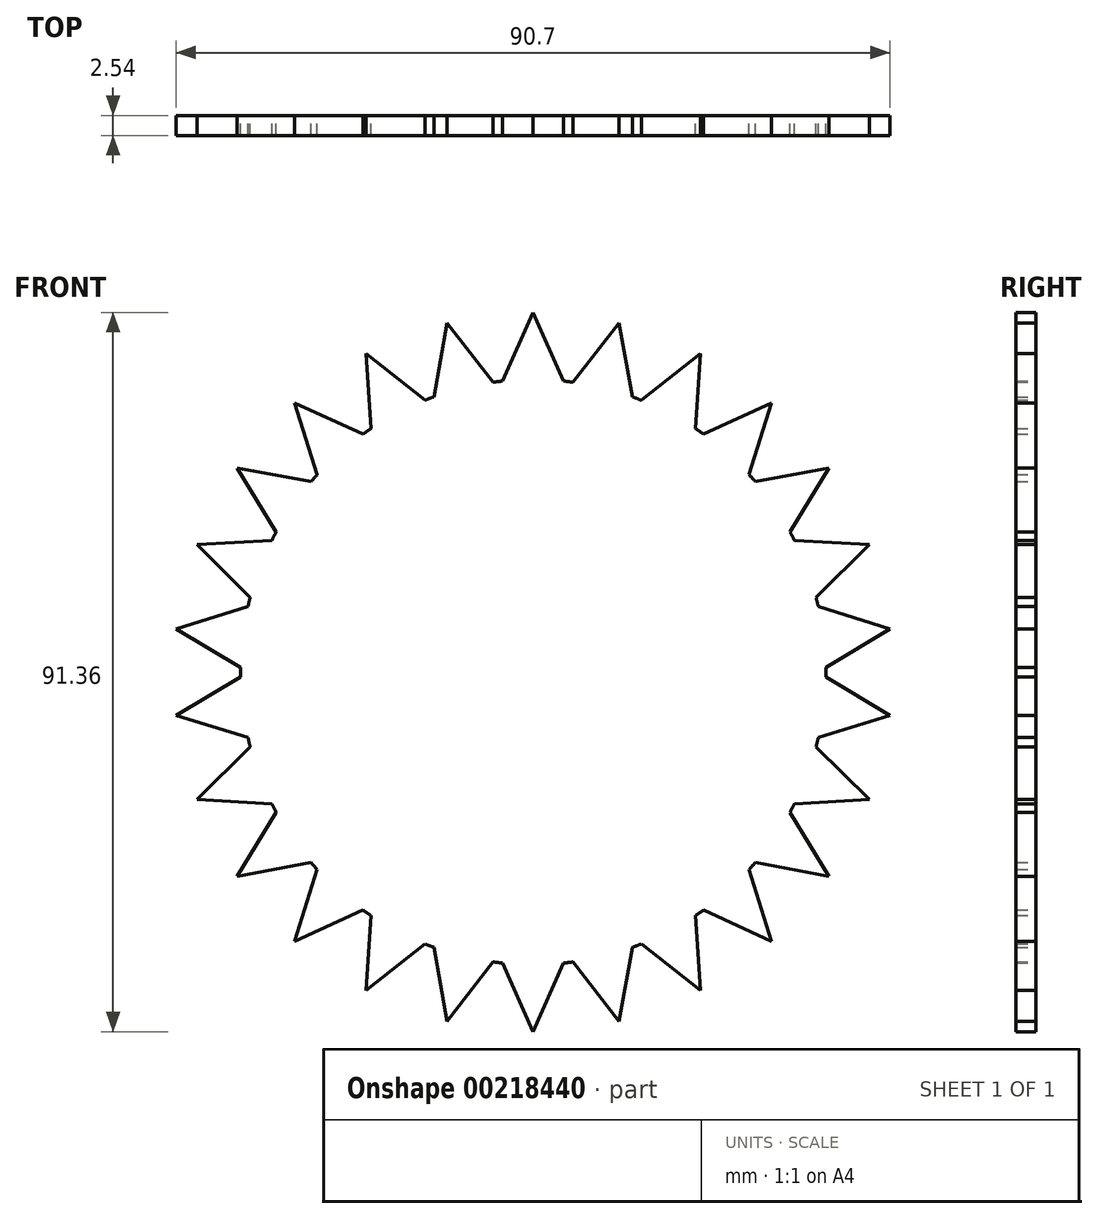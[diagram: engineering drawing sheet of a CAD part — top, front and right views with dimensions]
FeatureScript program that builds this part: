
annotation { "Feature Type Name" : "Feature", "Feature Type Description" : "" }
export const myFeature = defineFeature(function(context is Context, id is Id, definition is map)
    precondition{}
    {
        {
            var Q0;
            Q0=qCreatedBy(makeId("Front.planeOp"),FACE);
            var sketch = newSketch(context, id + "F0", { "sketchPlane" : qUnion([Q0])});
            skCircle(sketch, "E0", {"center": v(0, 0) * mm, "radius": 37.17 * mm});
            skLineSegment(sketch, "E1", {"start": v(0, 45.68) * mm, "end": v(3.88, 36.97) * mm});
            skLineSegment(sketch, "E2", {"start": v(0, 45.68) * mm, "end": v(-3.88, 36.97) * mm});
            skLineSegment(sketch, "E3.1.0", {"start": v(-10.93, 44.36) * mm, "end": v(-12.61, 34.96) * mm});
            skLineSegment(sketch, "E3.1.1", {"start": v(-10.93, 44.36) * mm, "end": v(-5.08, 36.82) * mm});
            skLineSegment(sketch, "E3.2.0", {"start": v(-21.23, 40.45) * mm, "end": v(-20.61, 30.93) * mm});
            skLineSegment(sketch, "E3.2.1", {"start": v(-21.23, 40.45) * mm, "end": v(-13.74, 34.53) * mm});
            skLineSegment(sketch, "E3.3.0", {"start": v(-30.3, 34.2) * mm, "end": v(-27.42, 25.1) * mm});
            skLineSegment(sketch, "E3.3.1", {"start": v(-30.3, 34.2) * mm, "end": v(-21.61, 30.24) * mm});
            skLineSegment(sketch, "E3.4.0", {"start": v(-37.6, 25.95) * mm, "end": v(-32.63, 17.8) * mm});
            skLineSegment(sketch, "E3.4.1", {"start": v(-37.6, 25.95) * mm, "end": v(-28.22, 24.2) * mm});
            skLineSegment(sketch, "E3.5.0", {"start": v(-42.71, 16.2) * mm, "end": v(-35.94, 9.48) * mm});
            skLineSegment(sketch, "E3.5.1", {"start": v(-42.71, 16.2) * mm, "end": v(-33.19, 16.74) * mm});
            skLineSegment(sketch, "E3.6.0", {"start": v(-45.35, 5.5) * mm, "end": v(-37.16, 0.6) * mm});
            skLineSegment(sketch, "E3.6.1", {"start": v(-45.35, 5.5) * mm, "end": v(-36.23, 8.3) * mm});
            skLineSegment(sketch, "E3.7.0", {"start": v(-45.35, -5.5) * mm, "end": v(-36.23, -8.3) * mm});
            skLineSegment(sketch, "E3.7.1", {"start": v(-45.35, -5.5) * mm, "end": v(-37.16, -0.6) * mm});
            skLineSegment(sketch, "E3.8.0", {"start": v(-42.71, -16.2) * mm, "end": v(-33.19, -16.74) * mm});
            skLineSegment(sketch, "E3.8.1", {"start": v(-42.71, -16.2) * mm, "end": v(-35.94, -9.48) * mm});
            skLineSegment(sketch, "E3.9.0", {"start": v(-37.6, -25.95) * mm, "end": v(-28.22, -24.2) * mm});
            skLineSegment(sketch, "E3.9.1", {"start": v(-37.6, -25.95) * mm, "end": v(-32.63, -17.8) * mm});
            skLineSegment(sketch, "E3.10.0", {"start": v(-30.3, -34.2) * mm, "end": v(-21.61, -30.24) * mm});
            skLineSegment(sketch, "E3.10.1", {"start": v(-30.3, -34.2) * mm, "end": v(-27.42, -25.1) * mm});
            skLineSegment(sketch, "E3.11.0", {"start": v(-21.23, -40.45) * mm, "end": v(-13.74, -34.53) * mm});
            skLineSegment(sketch, "E3.11.1", {"start": v(-21.23, -40.45) * mm, "end": v(-20.61, -30.93) * mm});
            skLineSegment(sketch, "E3.12.0", {"start": v(-10.93, -44.36) * mm, "end": v(-5.08, -36.82) * mm});
            skLineSegment(sketch, "E3.12.1", {"start": v(-10.93, -44.36) * mm, "end": v(-12.61, -34.96) * mm});
            skLineSegment(sketch, "E3.13.0", {"start": v(0, -45.68) * mm, "end": v(3.88, -36.97) * mm});
            skLineSegment(sketch, "E3.13.1", {"start": v(0, -45.68) * mm, "end": v(-3.88, -36.97) * mm});
            skLineSegment(sketch, "E3.14.0", {"start": v(10.93, -44.36) * mm, "end": v(12.61, -34.96) * mm});
            skLineSegment(sketch, "E3.14.1", {"start": v(10.93, -44.36) * mm, "end": v(5.08, -36.82) * mm});
            skLineSegment(sketch, "E3.15.0", {"start": v(21.23, -40.45) * mm, "end": v(20.61, -30.93) * mm});
            skLineSegment(sketch, "E3.15.1", {"start": v(21.23, -40.45) * mm, "end": v(13.74, -34.53) * mm});
            skLineSegment(sketch, "E3.16.0", {"start": v(30.3, -34.2) * mm, "end": v(27.42, -25.1) * mm});
            skLineSegment(sketch, "E3.16.1", {"start": v(30.3, -34.2) * mm, "end": v(21.61, -30.24) * mm});
            skLineSegment(sketch, "E3.17.0", {"start": v(37.6, -25.95) * mm, "end": v(32.63, -17.8) * mm});
            skLineSegment(sketch, "E3.17.1", {"start": v(37.6, -25.95) * mm, "end": v(28.22, -24.2) * mm});
            skLineSegment(sketch, "E3.18.0", {"start": v(42.71, -16.2) * mm, "end": v(35.94, -9.48) * mm});
            skLineSegment(sketch, "E3.18.1", {"start": v(42.71, -16.2) * mm, "end": v(33.19, -16.74) * mm});
            skLineSegment(sketch, "E3.19.0", {"start": v(45.35, -5.5) * mm, "end": v(37.16, -0.6) * mm});
            skLineSegment(sketch, "E3.19.1", {"start": v(45.35, -5.5) * mm, "end": v(36.23, -8.3) * mm});
            skLineSegment(sketch, "E3.20.0", {"start": v(45.35, 5.5) * mm, "end": v(36.23, 8.3) * mm});
            skLineSegment(sketch, "E3.20.1", {"start": v(45.35, 5.5) * mm, "end": v(37.16, 0.6) * mm});
            skLineSegment(sketch, "E3.21.0", {"start": v(42.71, 16.2) * mm, "end": v(33.19, 16.74) * mm});
            skLineSegment(sketch, "E3.21.1", {"start": v(42.71, 16.2) * mm, "end": v(35.94, 9.48) * mm});
            skLineSegment(sketch, "E3.22.0", {"start": v(37.6, 25.95) * mm, "end": v(28.22, 24.2) * mm});
            skLineSegment(sketch, "E3.22.1", {"start": v(37.6, 25.95) * mm, "end": v(32.63, 17.8) * mm});
            skLineSegment(sketch, "E3.23.0", {"start": v(30.3, 34.2) * mm, "end": v(21.61, 30.24) * mm});
            skLineSegment(sketch, "E3.23.1", {"start": v(30.3, 34.2) * mm, "end": v(27.42, 25.1) * mm});
            skLineSegment(sketch, "E3.24.0", {"start": v(21.23, 40.45) * mm, "end": v(13.74, 34.53) * mm});
            skLineSegment(sketch, "E3.24.1", {"start": v(21.23, 40.45) * mm, "end": v(20.61, 30.93) * mm});
            skLineSegment(sketch, "E3.25.0", {"start": v(10.93, 44.36) * mm, "end": v(5.08, 36.82) * mm});
            skLineSegment(sketch, "E3.25.1", {"start": v(10.93, 44.36) * mm, "end": v(12.61, 34.96) * mm});
            skSolve(sketch);
        }
        {
            var Q0;
            Q0 = qSketchRegion(id + "F0", true);
            extrude(context, id + "F1", {"entities" : qUnion([Q0]), "depth" : 2.54 * mm});
        }
    });
